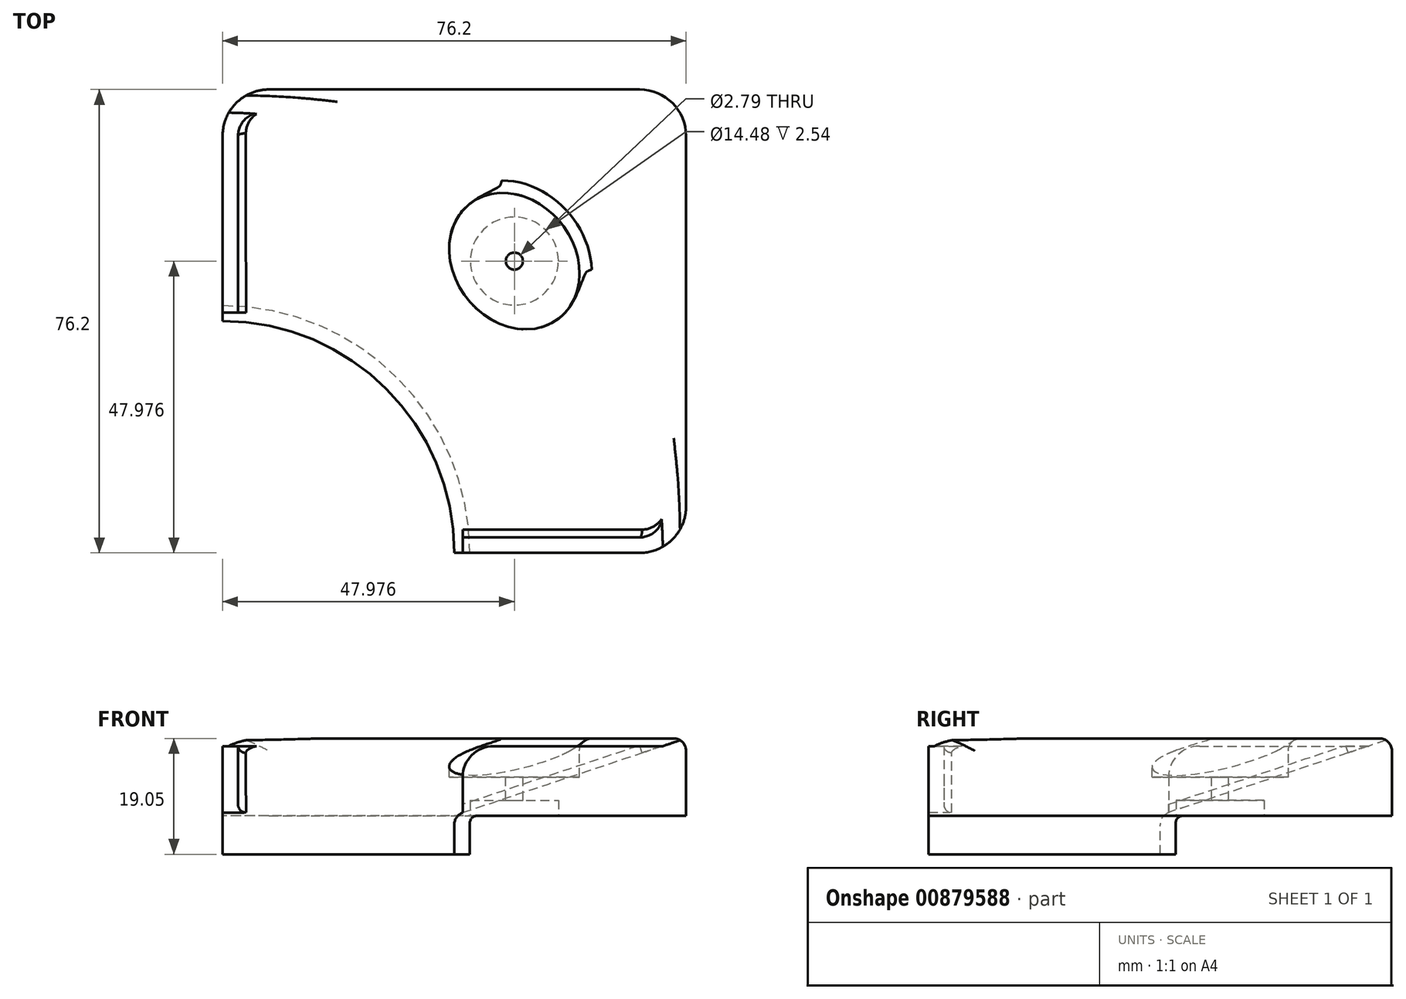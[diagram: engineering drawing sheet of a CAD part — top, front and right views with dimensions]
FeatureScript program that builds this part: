
annotation { "Feature Type Name" : "Feature", "Feature Type Description" : "" }
export const myFeature = defineFeature(function(context is Context, id is Id, definition is map)
    precondition{}
    {
        {
            var Q0;
            Q0=qCreatedBy(makeId("Top.planeOp"),FACE);
            var sketch = newSketch(context, id + "F0", { "sketchPlane" : qUnion([Q0])});
            skLineSegment(sketch, "E0.bottom", {"start": v(-38.1, 38.1) * mm, "end": v(38.1, 38.1) * mm});
            skLineSegment(sketch, "E0.top", {"start": v(0, -38.1) * mm, "end": v(38.1, -38.1) * mm});
            skLineSegment(sketch, "E0.left", {"start": v(-38.1, 38.1) * mm, "end": v(-38.1, 0) * mm});
            skLineSegment(sketch, "E0.right", {"start": v(38.1, 38.1) * mm, "end": v(38.1, -38.1) * mm});
            skPoint(sketch, "E0.middle", {"position": v(0, 0) * mm});
            skArc(sketch, "E1", {"start": v(0, -38.1) * mm, "mid": v(-11.16, -11.16) * mm, "end": v(-38.1, 0) * mm});
            skSolve(sketch);
        }
        {
            var Q0;
            Q0 = qSketchRegion(id + "F0", true);
            extrude(context, id + "F1", {"entities" : qUnion([Q0]), "depth" : 12.7 * mm, "offsetDistance" : 25.4 * mm});
        }
        {
            var Q0;
            Q0=makeQuery(id+"F1.opExtrude","SWEPT_FACE",FACE,{"disambiguationData":[OSD([sQuery(id+"F0.wireOp",EDGE,"E0.top")])]});
            var sketch = newSketch(context, id + "F2", { "sketchPlane" : qUnion([Q0])});
            skLineSegment(sketch, "E2", {"start": v(0, 0) * mm, "end": v(38.1, 12.7) * mm});
            skArc(sketch, "E3", {"start": v(38.1, 12.7) * mm, "mid": v(10.24, 32.78) * mm, "end": v(0, 0) * mm});
            skSolve(sketch);
        }
        {
            var Q0;
            Q0=qCreatedBy(makeId("Front.planeOp"),FACE);
            cPlane(context, id + "F3", {"entities" : qUnion([Q0]), "cplaneType" : CPlaneType.OFFSET, "offset" : 38.1 * mm, "width" : 152.4 * mm, "height" : 152.4 * mm});
        }
        {
            var Q0;
            Q0=qCreatedBy(id+"F3.planeOp",FACE);
            var sketch = newSketch(context, id + "F4", { "sketchPlane" : qUnion([Q0])});
            skLineSegment(sketch, "E4", {"start": v(-38.1, 0) * mm, "end": v(-38.1, 37.45) * mm, "construction": true});
            skSolve(sketch);
        }
        {
            var Q0;
            Q0 = qSketchRegion(id + "F2", true);
            var Q1;
            Q1=sQuery(id+"F4.wireOp",EDGE,"E4");
            revolve(context, id + "F5", {"operationType" : NewBodyOperationType.REMOVE, "surfaceOperationType" : NewSurfaceOperationType.NEW, "entities" : qUnion([Q0]), "axis" : qUnion([Q1]), "revolveType" : RevolveType.FULL});
        }
        {
            var Q0;
            Q0=makeQuery(id+"F1.opExtrude","CAP_FACE",FACE,{"disambiguationData":[OSD([sQuery(id+"F0.wireOp",EDGE,"E0.bottom"),sQuery(id+"F0.wireOp",EDGE,"E0.top"),sQuery(id+"F0.wireOp",EDGE,"E0.left"),sQuery(id+"F0.wireOp",EDGE,"E0.right"),sQuery(id+"F0.wireOp",EDGE,"E1")])],"isStart":true});
            var sketch = newSketch(context, id + "F6", { "sketchPlane" : qUnion([Q0])});
            skArc(sketch, "E5.0", {"start": v(0, 38.1) * mm, "mid": v(-11.16, 11.16) * mm, "end": v(-38.1, 0) * mm});
            skArc(sketch, "E6.0", {"start": v(2.54, 38.1) * mm, "mid": v(-9.36, 9.36) * mm, "end": v(-38.1, -2.54) * mm});
            skLineSegment(sketch, "E7", {"start": v(-38.1, -2.54) * mm, "end": v(-38.1, 0) * mm});
            skLineSegment(sketch, "E8", {"start": v(2.54, 38.1) * mm, "end": v(0, 38.1) * mm});
            skSolve(sketch);
        }
        {
            var Q0;
            Q0 = qSketchRegion(id + "F6", true);
            extrude(context, id + "F7", {"entities" : qUnion([Q0]), "operationType" : NewBodyOperationType.ADD, "depth" : 6.35 * mm, "offsetDistance" : 25.4 * mm});
        }
        {
            var Q0;
            Q0=makeQuery(id+"F1.opExtrude","CAP_FACE",FACE,{"disambiguationData":[OSD([sQuery(id+"F0.wireOp",EDGE,"E0.bottom"),sQuery(id+"F0.wireOp",EDGE,"E0.top"),sQuery(id+"F0.wireOp",EDGE,"E0.left"),sQuery(id+"F0.wireOp",EDGE,"E0.right"),sQuery(id+"F0.wireOp",EDGE,"E1")])],"isStart":false});
            var sketch = newSketch(context, id + "F8", { "sketchPlane" : qUnion([Q0])});
            skEllipse(sketch, "E9", {"center": v(9.88, 9.88) * mm, "majorRadius": 11.94 * mm, "minorRadius": 9.9 * mm, "majorAxis": v(0.61, -0.79)});
            skLineSegment(sketch, "E10", {"start": v(38.1, 38.1) * mm, "end": v(0, 0) * mm, "construction": true});
            skSolve(sketch);
        }
        {
            var Q0;
            Q0 = qSketchRegion(id + "F8", true);
            extrude(context, id + "F9", {"entities" : qUnion([Q0]), "operationType" : NewBodyOperationType.REMOVE, "oppositeDirection" : true, "depth" : 6.35 * mm, "offsetDistance" : 25.4 * mm});
        }
        {
            var Q0;
            Q0=makeQuery(id+"F9.boolean.opBoolean","COPY",FACE,{"derivedFrom":makeQuery(id+"F9.opExtrude","CAP_FACE",FACE,{"disambiguationData":[OSD([sQuery(id+"F8.wireOp",EDGE,"E9")])],"isStart":false})});
            var sketch = newSketch(context, id + "F10", { "sketchPlane" : qUnion([Q0])});
            skCircle(sketch, "E11", {"center": v(9.88, 9.88) * mm, "radius": 1.4 * mm});
            skSolve(sketch);
        }
        {
            var Q0;
            Q0 = qSketchRegion(id + "F10", true);
            extrude(context, id + "F11", {"entities" : qUnion([Q0]), "operationType" : NewBodyOperationType.REMOVE, "endBound" : BoundingType.THROUGH_ALL, "oppositeDirection" : true, "depth" : 25.4 * mm, "offsetDistance" : 25.4 * mm});
        }
        {
            var Q0;
            Q0=makeQuery(id+"F1.opExtrude","CAP_FACE",FACE,{"disambiguationData":[OSD([sQuery(id+"F0.wireOp",EDGE,"E0.bottom"),sQuery(id+"F0.wireOp",EDGE,"E0.top"),sQuery(id+"F0.wireOp",EDGE,"E0.left"),sQuery(id+"F0.wireOp",EDGE,"E0.right"),sQuery(id+"F0.wireOp",EDGE,"E1")])],"isStart":true});
            var sketch = newSketch(context, id + "F12", { "sketchPlane" : qUnion([Q0])});
            skCircle(sketch, "E12", {"center": v(9.88, -9.88) * mm, "radius": 7.24 * mm});
            skSolve(sketch);
        }
        {
            var Q0;
            Q0 = qSketchRegion(id + "F12", true);
            extrude(context, id + "F13", {"entities" : qUnion([Q0]), "operationType" : NewBodyOperationType.REMOVE, "oppositeDirection" : true, "depth" : 2.54 * mm, "offsetDistance" : 25.4 * mm});
        }
        {
            var Q0;
            Q0=makeQuery(id+"F1.opExtrude","SWEPT_EDGE",EDGE,{"disambiguationData":[OSD([sQuery(id+"F0.wireOp",EDGE,"E0.bottom"),sQuery(id+"F0.wireOp",EDGE,"E0.right")])]});
            var Q1;
            Q1=makeQuery(id+"F1.opExtrude","SWEPT_EDGE",EDGE,{"disambiguationData":[OSD([sQuery(id+"F0.wireOp",EDGE,"E0.bottom"),sQuery(id+"F0.wireOp",EDGE,"E0.left")])]});
            var Q2;
            Q2=makeQuery(id+"F1.opExtrude","SWEPT_EDGE",EDGE,{"disambiguationData":[OSD([sQuery(id+"F0.wireOp",EDGE,"E0.top"),sQuery(id+"F0.wireOp",EDGE,"E0.right")])]});
            fillet(context, id + "F14", {"entities" : qUnion([Q0, Q1, Q2]), "radius" : 7.62 * mm, "tangentPropagation" : true, "allowEdgeOverflow" : false});
        }
        {
            var Q0;
            Q0=makeQuery(id+"F1.opExtrude","CAP_FACE",FACE,{"disambiguationData":[OSD([sQuery(id+"F0.wireOp",EDGE,"E0.bottom"),sQuery(id+"F0.wireOp",EDGE,"E0.top"),sQuery(id+"F0.wireOp",EDGE,"E0.left"),sQuery(id+"F0.wireOp",EDGE,"E0.right"),sQuery(id+"F0.wireOp",EDGE,"E1")])],"isStart":false});
            var Q1;
            {var subQ0=sQuery(id+"F0.wireOp",EDGE,"E1");Q1=makeQuery(id+"F7.boolean.opBoolean","MERGE",EDGE,{"derivedFrom":[makeQuery(id+"F5.boolean.opBoolean","MERGE",EDGE,{"derivedFrom":[makeQuery(id+"F1.opExtrude","CAP_EDGE",EDGE,{"disambiguationData":[OSD([subQ0])],"isStart":true})],"fromTools":[makeQuery(id+"F5.opRevolve","SWEPT_EDGE",EDGE,{"disambiguationData":[OSD([sQuery(id+"F0.wireOp",EDGE,"E0.top"),subQ0,sQuery(id+"F2.wireOp",EDGE,"E2"),sQuery(id+"F2.wireOp",EDGE,"E3")])]})]}),makeQuery(id+"F7.opExtrude","CAP_EDGE",EDGE,{"disambiguationData":[OSD([sQuery(id+"F6.wireOp",EDGE,"E5.0")])],"isStart":true})]});}
            fillet(context, id + "F15", {"entities" : qUnion([Q0, Q1]), "radius" : 2.03 * mm, "tangentPropagation" : true, "allowEdgeOverflow" : false});
        }
        {
            var Q0;
            Q0=qCreatedBy(makeId("Top.planeOp"),FACE);
            var sketch = newSketch(context, id + "F16", { "sketchPlane" : qUnion([Q0])});
            skArc(sketch, "E13.0", {"start": v(-34.22, 37.12) * mm, "mid": v(-37.06, 34.33) * mm, "end": v(-38.1, 30.48) * mm});
            skLineSegment(sketch, "E14.0", {"start": v(-38.1, 1.39) * mm, "end": v(-38.1, 30.48) * mm});
            skLineSegment(sketch, "E15.0", {"start": v(30.48, -38.1) * mm, "end": v(1.39, -38.1) * mm});
            skArc(sketch, "E16.0", {"start": v(30.48, -38.1) * mm, "mid": v(34.33, -37.06) * mm, "end": v(37.12, -34.22) * mm});
            skLineSegment(sketch, "E17.0", {"start": v(-35.56, 1.39) * mm, "end": v(-35.56, 30.48) * mm});
            skArc(sketch, "E17.1", {"start": v(-32.97, 34.9) * mm, "mid": v(-34.87, 33.04) * mm, "end": v(-35.56, 30.48) * mm});
            skLineSegment(sketch, "E18.0", {"start": v(30.48, -35.56) * mm, "end": v(1.39, -35.56) * mm});
            skArc(sketch, "E18.1", {"start": v(30.48, -35.56) * mm, "mid": v(33.04, -34.87) * mm, "end": v(34.9, -32.97) * mm});
            skLineSegment(sketch, "E19", {"start": v(-32.97, 34.9) * mm, "end": v(-34.22, 37.12) * mm});
            skLineSegment(sketch, "E20", {"start": v(-38.1, 1.39) * mm, "end": v(-35.56, 1.39) * mm});
            skLineSegment(sketch, "E21", {"start": v(34.9, -32.97) * mm, "end": v(37.12, -34.22) * mm});
            skLineSegment(sketch, "E22", {"start": v(1.39, -35.56) * mm, "end": v(1.39, -38.1) * mm});
            skSolve(sketch);
        }
        {
            var Q0;
            Q0 = qSketchRegion(id + "F16", true);
            extrude(context, id + "F17", {"entities" : qUnion([Q0]), "operationType" : NewBodyOperationType.ADD, "depth" : 11.43 * mm, "offsetDistance" : 25.4 * mm});
        }
        {
            var Q0;
            Q0=makeQuery(id+"F17.opExtrude","CAP_EDGE",EDGE,{"disambiguationData":[OSD([sQuery(id+"F16.wireOp",EDGE,"E22")])],"isStart":false});
            var Q1;
            Q1=makeQuery(id+"F17.opExtrude","CAP_EDGE",EDGE,{"disambiguationData":[OSD([sQuery(id+"F16.wireOp",EDGE,"E20")])],"isStart":false});
            fillet(context, id + "F18", {"entities" : qUnion([Q0, Q1]), "radius" : 5.08 * mm, "tangentPropagation" : true, "allowEdgeOverflow" : false});
        }
        {
            var Q0;
            Q0=makeQuery(id+"F17.boolean.opBoolean","INTERSECT",EDGE,{"derivedFrom":[makeQuery(id+"F17.opExtrude","CAP_FACE",FACE,{"disambiguationData":[OSD([sQuery(id+"F16.wireOp",EDGE,"E13.0"),sQuery(id+"F16.wireOp",EDGE,"E14.0"),sQuery(id+"F16.wireOp",EDGE,"E17.0"),sQuery(id+"F16.wireOp",EDGE,"E17.1"),sQuery(id+"F16.wireOp",EDGE,"E19"),sQuery(id+"F16.wireOp",EDGE,"E20")])],"isStart":true}),makeQuery(id+"F17.opExtrude","CAP_FACE",FACE,{"disambiguationData":[OSD([sQuery(id+"F16.wireOp",EDGE,"E15.0"),sQuery(id+"F16.wireOp",EDGE,"E16.0"),sQuery(id+"F16.wireOp",EDGE,"E18.0"),sQuery(id+"F16.wireOp",EDGE,"E18.1"),sQuery(id+"F16.wireOp",EDGE,"E21"),sQuery(id+"F16.wireOp",EDGE,"E22")])],"isStart":true})]});
            fillet(context, id + "F19", {"entities" : qUnion([Q0]), "radius" : 1.27 * mm, "tangentPropagation" : true, "allowEdgeOverflow" : false});
        }
        {
            var Q0;
            Q0=makeQuery(id+"F17.boolean.opBoolean","INTERSECT",EDGE,{"derivedFrom":[makeQuery(id+"F5.boolean.opBoolean","COPY",FACE,{"derivedFrom":makeQuery(id+"F5.opRevolve","SWEPT_FACE",FACE,{"disambiguationData":[OSD([sQuery(id+"F2.wireOp",EDGE,"E2")])]})}),makeQuery(id+"F17.opExtrude","SWEPT_FACE",FACE,{"disambiguationData":[OSD([sQuery(id+"F16.wireOp",EDGE,"E17.0")])]})]});
            var Q1;
            Q1=makeQuery(id+"F17.boolean.opBoolean","INTERSECT",EDGE,{"derivedFrom":[makeQuery(id+"F5.boolean.opBoolean","COPY",FACE,{"derivedFrom":makeQuery(id+"F5.opRevolve","SWEPT_FACE",FACE,{"disambiguationData":[OSD([sQuery(id+"F2.wireOp",EDGE,"E2")])]})}),makeQuery(id+"F17.opExtrude","SWEPT_FACE",FACE,{"disambiguationData":[OSD([sQuery(id+"F16.wireOp",EDGE,"E17.1")])]})]});
            var Q2;
            Q2=makeQuery(id+"F17.boolean.opBoolean","INTERSECT",EDGE,{"derivedFrom":[makeQuery(id+"F5.boolean.opBoolean","COPY",FACE,{"derivedFrom":makeQuery(id+"F5.opRevolve","SWEPT_FACE",FACE,{"disambiguationData":[OSD([sQuery(id+"F2.wireOp",EDGE,"E2")])]})}),makeQuery(id+"F17.opExtrude","SWEPT_FACE",FACE,{"disambiguationData":[OSD([sQuery(id+"F16.wireOp",EDGE,"E18.0")])]})]});
            var Q3;
            Q3=makeQuery(id+"F17.boolean.opBoolean","INTERSECT",EDGE,{"derivedFrom":[makeQuery(id+"F5.boolean.opBoolean","COPY",FACE,{"derivedFrom":makeQuery(id+"F5.opRevolve","SWEPT_FACE",FACE,{"disambiguationData":[OSD([sQuery(id+"F2.wireOp",EDGE,"E2")])]})}),makeQuery(id+"F17.opExtrude","SWEPT_FACE",FACE,{"disambiguationData":[OSD([sQuery(id+"F16.wireOp",EDGE,"E18.1")])]})]});
            fillet(context, id + "F20", {"entities" : qUnion([Q0, Q1, Q2, Q3]), "radius" : 1.27 * mm, "tangentPropagation" : true, "allowEdgeOverflow" : false});
        }
    });
